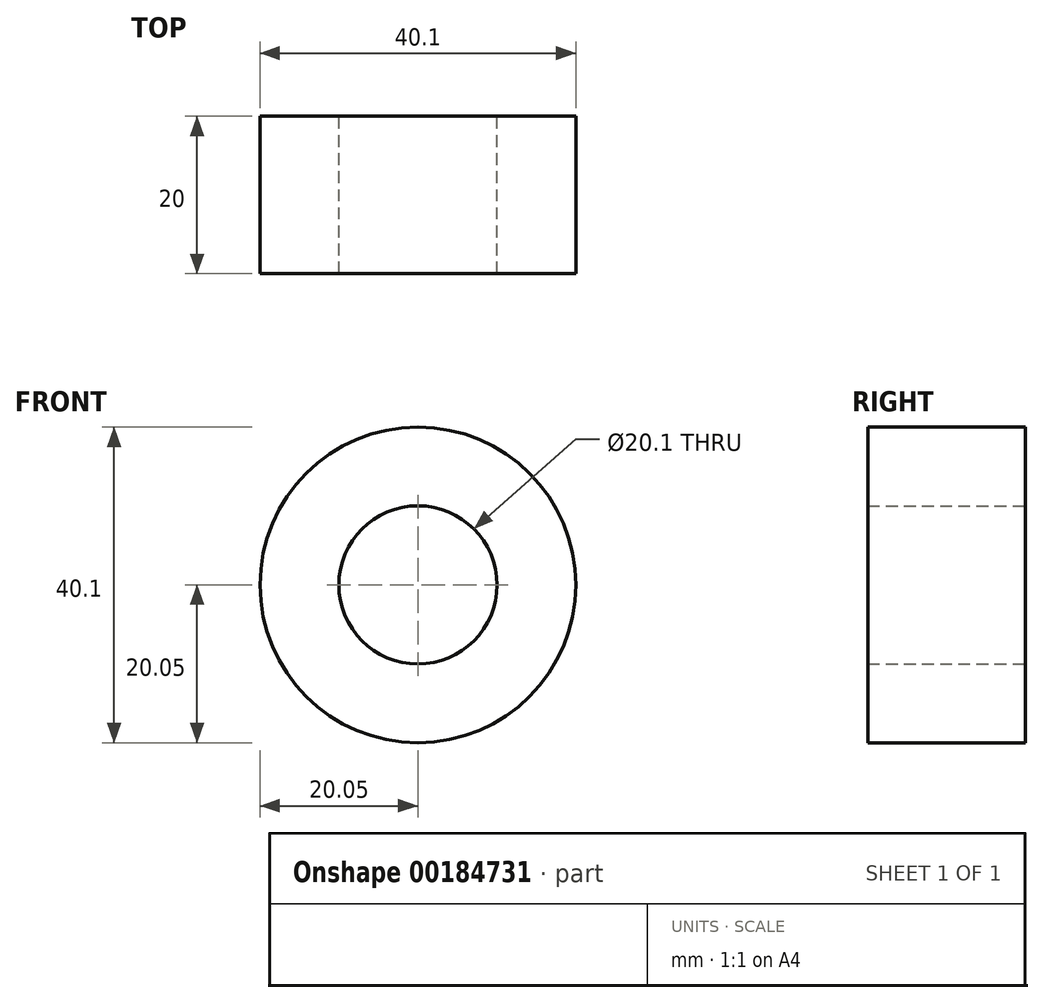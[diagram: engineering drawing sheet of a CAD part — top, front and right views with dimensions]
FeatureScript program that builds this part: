
annotation { "Feature Type Name" : "Feature", "Feature Type Description" : "" }
export const myFeature = defineFeature(function(context is Context, id is Id, definition is map)
    precondition{}
    {
        {
            var Q0;
            Q0=qCreatedBy(makeId("Front.planeOp"),FACE);
            var sketch = newSketch(context, id + "F0", { "sketchPlane" : qUnion([Q0])});
            skCircle(sketch, "E0", {"center": v(0, 0) * mm, "radius": 10.05 * mm});
            skCircle(sketch, "E1.0", {"center": v(0, 0) * mm, "radius": 20.05 * mm});
            skSolve(sketch);
        }
        {
            var Q0;
            Q0=makeQuery(id+"F0.imprint","IMPRINT",FACE,{"disambiguationData":[TD([[makeQuery(id+"F0.imprint","IMPRINT",EDGE,{"derivedFrom":sQuery(id+"F0.wireOp",EDGE,"E0")}),-1.0]])]});
            extrude(context, id + "F1", {"entities" : qUnion([Q0]), "endBound" : BoundingType.SYMMETRIC, "depth" : 20 * mm});
        }
    });
